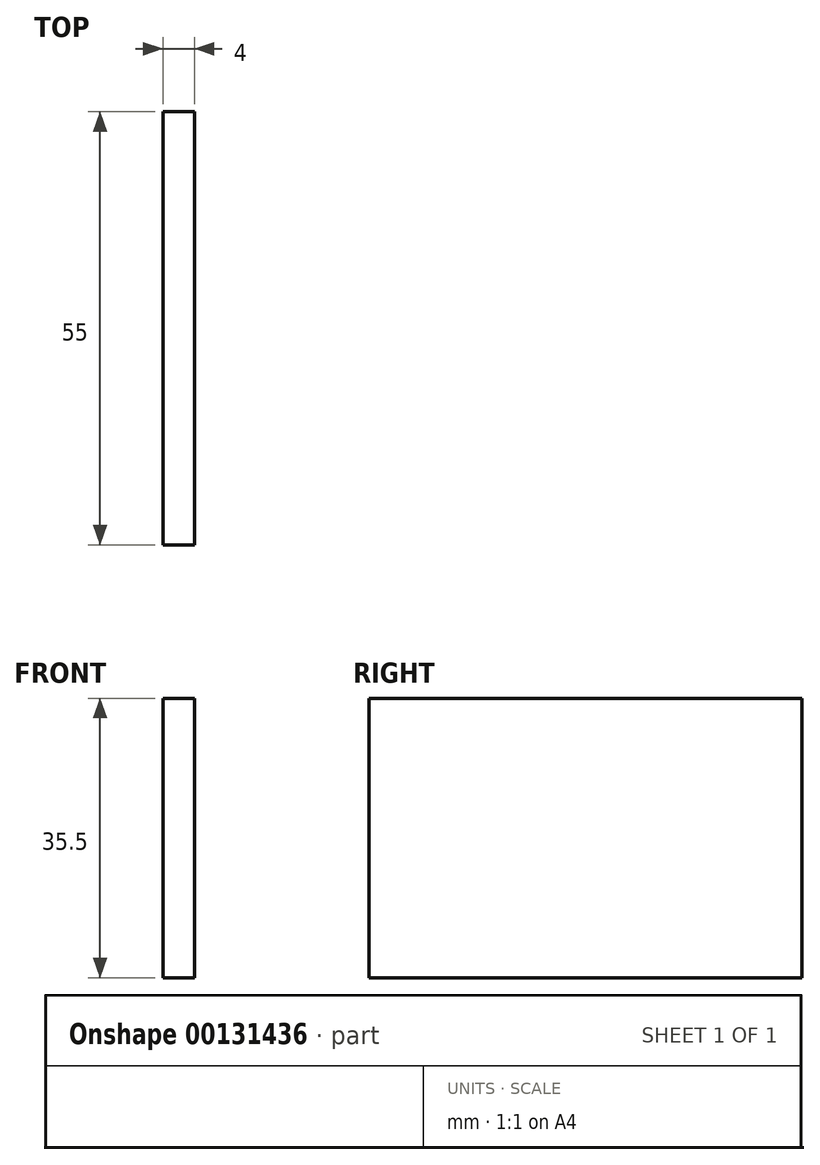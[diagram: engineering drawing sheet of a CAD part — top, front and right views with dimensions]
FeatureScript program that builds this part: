
annotation { "Feature Type Name" : "Feature", "Feature Type Description" : "" }
export const myFeature = defineFeature(function(context is Context, id is Id, definition is map)
    precondition{}
    {
        {
            var Q0;
            Q0=qCreatedBy(makeId("Top.planeOp"),FACE);
            var sketch = newSketch(context, id + "F0", { "sketchPlane" : qUnion([Q0])});
            skLineSegment(sketch, "E0.bottom", {"start": v(2, -27.5) * mm, "end": v(-2, -27.5) * mm});
            skLineSegment(sketch, "E0.top", {"start": v(2, 27.5) * mm, "end": v(-2, 27.5) * mm});
            skLineSegment(sketch, "E0.left", {"start": v(2, -27.5) * mm, "end": v(2, 27.5) * mm});
            skLineSegment(sketch, "E0.right", {"start": v(-2, -27.5) * mm, "end": v(-2, 27.5) * mm});
            skPoint(sketch, "E0.middle", {"position": v(0, 0) * mm});
            skLineSegment(sketch, "E1.bottom", {"start": v(-2, -27.5) * mm, "end": v(0, -27.5) * mm});
            skLineSegment(sketch, "E1.top", {"start": v(-2, -30) * mm, "end": v(0, -30) * mm});
            skLineSegment(sketch, "E1.left", {"start": v(-2, -27.5) * mm, "end": v(-2, -30) * mm});
            skLineSegment(sketch, "E1.right", {"start": v(0, -27.5) * mm, "end": v(0, -30) * mm});
            skLineSegment(sketch, "E2", {"start": v(0, -28.75) * mm, "end": v(2, -28.75) * mm});
            skLineSegment(sketch, "E3.bottom", {"start": v(-2, 27.5) * mm, "end": v(0, 27.5) * mm});
            skLineSegment(sketch, "E3.top", {"start": v(-2, 30) * mm, "end": v(0, 30) * mm});
            skLineSegment(sketch, "E3.left", {"start": v(-2, 27.5) * mm, "end": v(-2, 30) * mm});
            skLineSegment(sketch, "E3.right", {"start": v(0, 27.5) * mm, "end": v(0, 30) * mm});
            skLineSegment(sketch, "E4", {"start": v(0, 28.75) * mm, "end": v(2, 28.75) * mm});
            skSolve(sketch);
        }
        {
            var Q0;
            {var subQ3=sQuery(id+"F0.wireOp",EDGE,"E0.left");Q0=makeQuery(id+"F0.imprint","IMPRINT",FACE,{"disambiguationData":[TD([[makeQuery(id+"F0.imprint","IMPRINT",EDGE,{"derivedFrom":subQ3}),1.0]])]});}
            var Q1;
            {var subQ1=sQuery(id+"F0.wireOp",EDGE,"E3.bottom");Q1=makeQuery(id+"F0.imprint","IMPRINT",FACE,{"disambiguationData":[TD([[makeQuery(id+"F0.imprint","IMPRINT",EDGE,{"derivedFrom":subQ1}),1.0]])]});}
            var Q2;
            {var subQ1=sQuery(id+"F0.wireOp",EDGE,"E1.bottom");Q2=makeQuery(id+"F0.imprint","IMPRINT",FACE,{"disambiguationData":[TD([[makeQuery(id+"F0.imprint","IMPRINT",EDGE,{"derivedFrom":subQ1}),-1.0]])]});}
            extrude(context, id + "F1", {"entities" : qUnion([Q0, Q1, Q2]), "oppositeDirection" : true, "depth" : 35.5 * mm});
        }
    });
